annotation { "Feature Type Name" : "Feature", "Feature Type Description" : "" }
export const myFeature = defineFeature(function(context is Context, id is Id, definition is map)
    precondition{}
    {
        {
            var Q0;
            Q0=qCreatedBy(makeId("Top.planeOp"),FACE);
            var sketch = newSketch(context, id + "F0", { "sketchPlane" : qUnion([Q0])});
            skLineSegment(sketch, "E0.bottom", {"start": v(-45.35, 37.16) * mm, "end": v(51.76, 37.16) * mm});
            skLineSegment(sketch, "E0.top", {"start": v(-45.35, -33.37) * mm, "end": v(51.76, -33.37) * mm});
            skLineSegment(sketch, "E0.left", {"start": v(-50.43, 32.08) * mm, "end": v(-50.43, -28.3) * mm});
            skLineSegment(sketch, "E0.right", {"start": v(56.84, 32.08) * mm, "end": v(56.84, -28.3) * mm});
            skPoint(sketch, "E1.visualSharp", {"position": v(-50.43, 37.16) * mm});
            skArc(sketch, "E1.filletArc", {"start": v(-45.35, 37.16) * mm, "mid": v(-48.94, 35.68) * mm, "end": v(-50.43, 32.08) * mm});
            skPoint(sketch, "E2.visualSharp", {"position": v(56.84, 37.16) * mm});
            skArc(sketch, "E2.filletArc", {"start": v(56.84, 32.08) * mm, "mid": v(55.35, 35.68) * mm, "end": v(51.76, 37.16) * mm});
            skPoint(sketch, "E3.visualSharp", {"position": v(56.84, -33.37) * mm});
            skArc(sketch, "E3.filletArc", {"start": v(51.76, -33.37) * mm, "mid": v(55.35, -31.89) * mm, "end": v(56.84, -28.3) * mm});
            skPoint(sketch, "E4.visualSharp", {"position": v(-50.43, -33.37) * mm});
            skArc(sketch, "E4.filletArc", {"start": v(-50.43, -28.3) * mm, "mid": v(-48.94, -31.89) * mm, "end": v(-45.35, -33.37) * mm});
            skSolve(sketch);
        }
        {
            var Q0;
            Q0 = qSketchRegion(id + "F0", true);
            extrude(context, id + "F1", {"entities" : qUnion([Q0]), "depth" : 3.56 * mm});
        }
        {
            var Q0;
            Q0=qCreatedBy(makeId("Top.planeOp"),FACE);
            var sketch = newSketch(context, id + "F2", { "sketchPlane" : qUnion([Q0])});
            skLineSegment(sketch, "E5", {"start": v(-36.18, 33.46) * mm, "end": v(37, 33.46) * mm});
            skLineSegment(sketch, "E6", {"start": v(37, 33.46) * mm, "end": v(38.02, 33.04) * mm});
            skLineSegment(sketch, "E7", {"start": v(38.02, 33.04) * mm, "end": v(38.46, 32.16) * mm});
            skLineSegment(sketch, "E8", {"start": v(38.46, 32.16) * mm, "end": v(38.46, 31.23) * mm});
            skLineSegment(sketch, "E9", {"start": v(38.46, 31.23) * mm, "end": v(38.02, 30.6) * mm});
            skLineSegment(sketch, "E10", {"start": v(38.02, 30.6) * mm, "end": v(37, 30.2) * mm});
            skLineSegment(sketch, "E11", {"start": v(37, 30.2) * mm, "end": v(-36.18, 30.2) * mm});
            skLineSegment(sketch, "E12", {"start": v(-36.18, 30.2) * mm, "end": v(-37.12, 30.91) * mm});
            skPoint(sketch, "E12.endSnap0", {"position": v(38.24, 30.91) * mm});
            skLineSegment(sketch, "E13", {"start": v(-37.12, 30.91) * mm, "end": v(-37.12, 32.2) * mm});
            skLineSegment(sketch, "E14", {"start": v(-37.12, 32.2) * mm, "end": v(-36.18, 33.46) * mm});
            skSolve(sketch);
        }
        {
            var Q0;
            Q0 = qSketchRegion(id + "F2", true);
            extrude(context, id + "F3", {"entities" : qUnion([Q0]), "operationType" : NewBodyOperationType.REMOVE, "depth" : 12.45 * mm, "hasSecondDirection" : true, "secondDirectionOppositeDirection" : false, "secondDirectionDepth" : 2.03 * mm});
        }
        {
            var Q0;
            Q0=qCreatedBy(makeId("Top.planeOp"),FACE);
            var sketch = newSketch(context, id + "F4", { "sketchPlane" : qUnion([Q0])});
            skLineSegment(sketch, "E15.bottom", {"start": v(-34.8, 7.88) * mm, "end": v(39.13, 7.88) * mm});
            skLineSegment(sketch, "E15.top", {"start": v(-34.8, -8.67) * mm, "end": v(39.13, -8.67) * mm});
            skLineSegment(sketch, "E15.left", {"start": v(-34.8, 7.88) * mm, "end": v(-34.8, -8.67) * mm});
            skLineSegment(sketch, "E15.right", {"start": v(39.13, 7.88) * mm, "end": v(39.13, -8.67) * mm});
            skLineSegment(sketch, "E16.bottom", {"start": v(-32.23, 4.87) * mm, "end": v(36.98, 4.87) * mm});
            skLineSegment(sketch, "E16.top", {"start": v(-32.23, -6.52) * mm, "end": v(36.98, -6.52) * mm});
            skLineSegment(sketch, "E16.left", {"start": v(-32.23, 4.87) * mm, "end": v(-32.23, -6.52) * mm});
            skLineSegment(sketch, "E16.right", {"start": v(36.98, 4.87) * mm, "end": v(36.98, -6.52) * mm});
            skSolve(sketch);
        }
        {
            var Q0;
            Q0 = qSketchRegion(id + "F4", true);
            extrude(context, id + "F5", {"entities" : qUnion([Q0]), "operationType" : NewBodyOperationType.REMOVE, "depth" : 12.2 * mm, "hasSecondDirection" : true, "secondDirectionOppositeDirection" : false, "secondDirectionDepth" : 1.78 * mm});
        }
        {
            var Q0;
            Q0=qCreatedBy(makeId("Top.planeOp"),FACE);
            var sketch = newSketch(context, id + "F6", { "sketchPlane" : qUnion([Q0])});
            skText(sketch, "E17", { "text": "POINT GREY", "fontName": "OpenSans-Regular.ttf"});
            const initialGuessF6  = {"E17": [-0.03254, -0.00537, 1, 0, 0.00858]};
            skSetInitialGuess(sketch, initialGuessF6);
            skSolve(sketch);
        }
        {
            var Q0;
            Q0 = qSketchRegion(id + "F6", true);
            extrude(context, id + "F7", {"entities" : qUnion([Q0]), "operationType" : NewBodyOperationType.REMOVE, "depth" : 13.2 * mm, "hasSecondDirection" : true, "secondDirectionOppositeDirection" : false, "secondDirectionDepth" : 1.27 * mm});
        }
    });